# Revit family: BLE-G-WHB-G6-LED
name_source: partatom
category: Lighting Fixtures
units: mm (PartAtom-declared; Revit-internal decimal feet)

## family parameters
Cut with Voids When Loaded = No
Host = Face
Light Source = Yes
Maintain Annotation Orientation = No
Part Type = Normal
Room Calculation Point = No
Round Connector Dimension = Use Diameter
Shared = No

## types (8) — shared parameters
Base Material = 100 - Black
Color Filter = 16777215
Default Elevation = 4' - 0"
Dimming Lamp Color Temperature Shift = <None>
Gooseneck Material = 100 - Black
Photometric Web File = generic
Shade Material = 100 - Black
Tilt Angle = 0.00°

## per-type parameters (varying)
| type | 11" | 13" | 15" | 17" | Dome | Flat | Heat Sink | Heat Sink 6" | Heat Sink 9" |
| 11" Dome | Yes | No | No | No | Yes | No | 0' - 3 19/32" | Yes | No |
| 13" Dome | No | Yes | No | No | Yes | No | 0' - 4" | No | Yes |
| 15" Dome | No | No | Yes | No | Yes | No | 0' - 3 29/32" | No | Yes |
| 17" Dome | No | No | No | Yes | Yes | No | 0' - 3 29/32" | No | Yes |
| 11" Flat | Yes | No | No | No | No | Yes | 0' - 3 19/32" | Yes | No |
| 13" Flat | No | Yes | No | No | No | Yes | 0' - 4" | No | Yes |
| 15" Flat | No | No | Yes | No | No | Yes | 0' - 3 29/32" | No | Yes |
| 17" Flat | No | No | No | Yes | No | Yes | 0' - 3 29/32" | No | Yes |

## geometry (parser evidence)
native form markers: Sweep x38
no freeform markers — native parametric forms only
